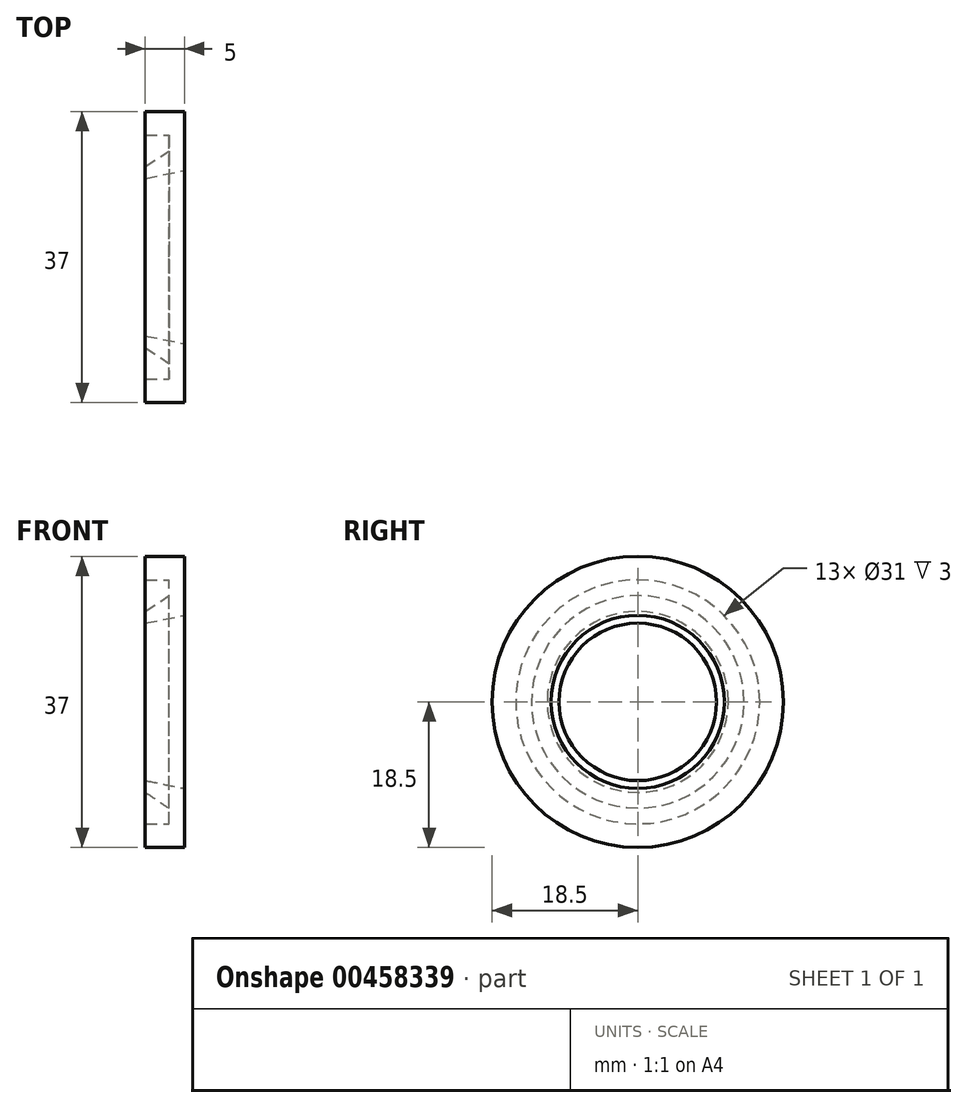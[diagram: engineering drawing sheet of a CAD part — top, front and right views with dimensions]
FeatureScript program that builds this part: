
annotation { "Feature Type Name" : "Feature", "Feature Type Description" : "" }
export const myFeature = defineFeature(function(context is Context, id is Id, definition is map)
    precondition{}
    {
        {
            var Q0;
            Q0=qCreatedBy(makeId("Top.planeOp"),FACE);
            var sketch = newSketch(context, id + "F0", { "sketchPlane" : qUnion([Q0])});
            skLineSegment(sketch, "E0", {"start": v(0, 0) * mm, "end": v(-11, 0) * mm, "construction": true});
            skLineSegment(sketch, "E1", {"start": v(0, 11) * mm, "end": v(0, 18.5) * mm});
            skLineSegment(sketch, "E2", {"start": v(0, 18.5) * mm, "end": v(-5, 18.5) * mm});
            skLineSegment(sketch, "E3", {"start": v(-5, 18.5) * mm, "end": v(-5, 15.5) * mm});
            skLineSegment(sketch, "E4", {"start": v(-5, 15.5) * mm, "end": v(-2, 15.5) * mm});
            skLineSegment(sketch, "E5", {"start": v(-2, 15.5) * mm, "end": v(-2, 13.5) * mm});
            skLineSegment(sketch, "E6", {"start": v(-5, 11.5) * mm, "end": v(-2, 13.5) * mm});
            skLineSegment(sketch, "E7", {"start": v(-5, 11.5) * mm, "end": v(-5, 10) * mm});
            skLineSegment(sketch, "E8", {"start": v(0, 11) * mm, "end": v(-5, 10) * mm});
            skSolve(sketch);
        }
        {
            var Q0;
            Q0=makeQuery(id+"F0.imprint","IMPRINT",FACE,{"disambiguationData":[TD([[makeQuery(id+"F0.imprint","IMPRINT",EDGE,{"derivedFrom":sQuery(id+"F0.wireOp",EDGE,"E1")}),1.0]])]});
            var Q1;
            Q1=sQuery(id+"F0.wireOp",EDGE,"E0");
            revolve(context, id + "F1", {"entities" : qUnion([Q0]), "axis" : qUnion([Q1]), "revolveType" : RevolveType.FULL});
        }
    });
